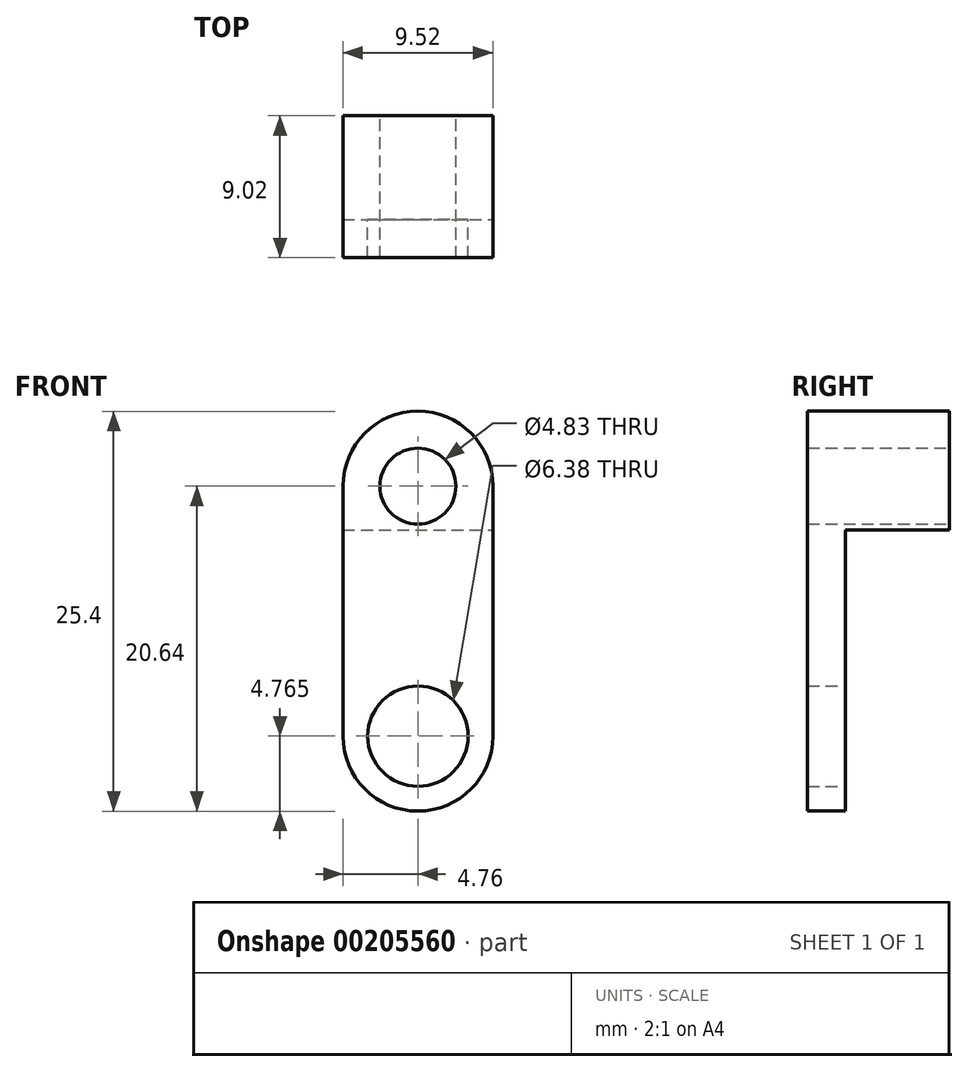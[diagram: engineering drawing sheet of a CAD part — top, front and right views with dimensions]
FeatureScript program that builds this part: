
annotation { "Feature Type Name" : "Feature", "Feature Type Description" : "" }
export const myFeature = defineFeature(function(context is Context, id is Id, definition is map)
    precondition{}
    {
        {
            var Q0;
            Q0=qCreatedBy(makeId("Front.planeOp"),FACE);
            var sketch = newSketch(context, id + "F0", { "sketchPlane" : qUnion([Q0])});
            skCircle(sketch, "E0", {"center": v(0, 0) * mm, "radius": 4.76 * mm});
            skCircle(sketch, "E1", {"center": v(0, -15.88) * mm, "radius": 4.76 * mm});
            skLineSegment(sketch, "E2", {"start": v(-4.76, 0) * mm, "end": v(-4.76, -15.88) * mm});
            skLineSegment(sketch, "E3", {"start": v(4.76, 0) * mm, "end": v(4.76, -15.88) * mm});
            skCircle(sketch, "E4", {"center": v(0, 0) * mm, "radius": 2.41 * mm});
            skCircle(sketch, "E5", {"center": v(0, -15.88) * mm, "radius": 3.19 * mm});
            skSolve(sketch);
        }
        {
            var Q0;
            Q0=qSketchRegion(id+"F0",true);
            extrude(context, id + "F1", {"entities" : qUnion([Q0]), "depth" : 9.02 * mm});
        }
        {
            var Q0;
            Q0=makeQuery(id+"F1.opExtrude","SWEPT_FACE",FACE,{"disambiguationData":[OSD([sQuery(id+"F0.wireOp",EDGE,"E3")])]});
            var sketch = newSketch(context, id + "F2", { "sketchPlane" : qUnion([Q0])});
            skLineSegment(sketch, "E6.bottom", {"start": v(-6.6, -2.8) * mm, "end": v(9.73, -2.8) * mm});
            skLineSegment(sketch, "E6.top", {"start": v(-6.6, -21.31) * mm, "end": v(9.73, -21.31) * mm});
            skLineSegment(sketch, "E6.left", {"start": v(-6.6, -2.8) * mm, "end": v(-6.6, -21.31) * mm});
            skLineSegment(sketch, "E6.right", {"start": v(9.73, -2.8) * mm, "end": v(9.73, -21.31) * mm});
            skSolve(sketch);
        }
        {
            var Q0;
            Q0=qSketchRegion(id+"F2",true);
            extrude(context, id + "F3", {"entities" : qUnion([Q0]), "operationType" : NewBodyOperationType.REMOVE, "endBound" : BoundingType.THROUGH_ALL, "oppositeDirection" : true, "depth" : 25.4 * mm});
        }
    });
